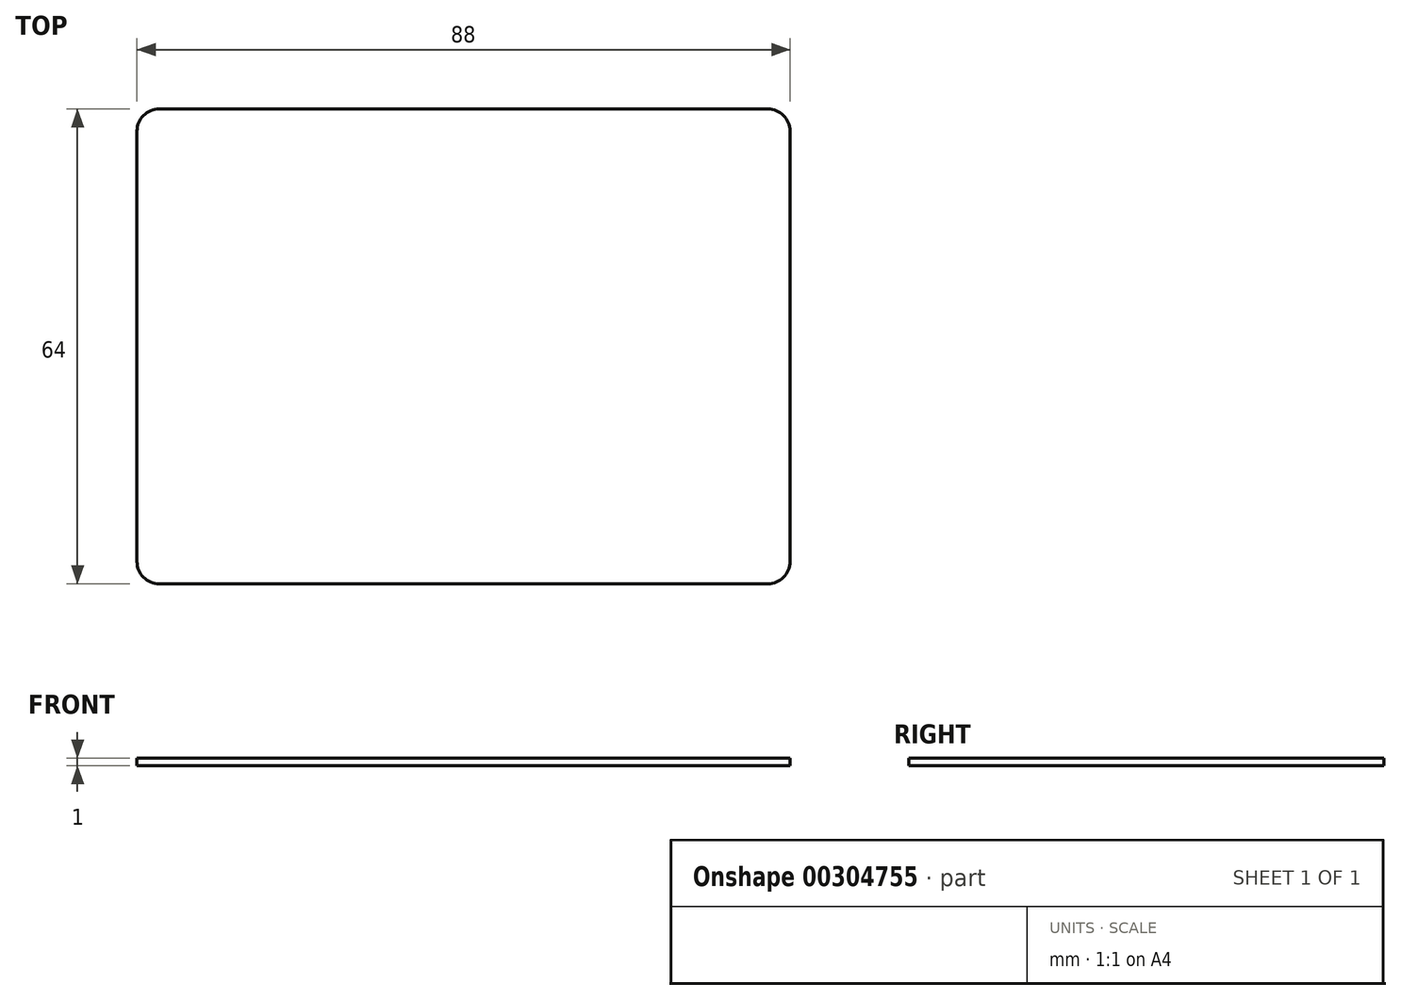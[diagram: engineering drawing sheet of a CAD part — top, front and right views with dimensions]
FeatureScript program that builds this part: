
annotation { "Feature Type Name" : "Feature", "Feature Type Description" : "" }
export const myFeature = defineFeature(function(context is Context, id is Id, definition is map)
    precondition{}
    {
        {
            var Q0;
            Q0=qCreatedBy(makeId("Top.planeOp"),FACE);
            var sketch = newSketch(context, id + "F0", { "sketchPlane" : qUnion([Q0])});
            skLineSegment(sketch, "E0.bottom", {"start": v(41, -32) * mm, "end": v(-41, -32) * mm});
            skLineSegment(sketch, "E0.top", {"start": v(41, 32) * mm, "end": v(-41, 32) * mm});
            skLineSegment(sketch, "E0.left", {"start": v(44, -29) * mm, "end": v(44, 29) * mm});
            skLineSegment(sketch, "E0.right", {"start": v(-44, -29) * mm, "end": v(-44, 29) * mm});
            skPoint(sketch, "E0.middle", {"position": v(0, 0) * mm});
            skPoint(sketch, "E1.visualSharp", {"position": v(-44, 32) * mm});
            skArc(sketch, "E1.filletArc", {"start": v(-41, 32) * mm, "mid": v(-43.12, 31.12) * mm, "end": v(-44, 29) * mm});
            skPoint(sketch, "E2.visualSharp", {"position": v(-44, -32) * mm});
            skArc(sketch, "E2.filletArc", {"start": v(-44, -29) * mm, "mid": v(-43.12, -31.12) * mm, "end": v(-41, -32) * mm});
            skPoint(sketch, "E3.visualSharp", {"position": v(44, -32) * mm});
            skArc(sketch, "E3.filletArc", {"start": v(41, -32) * mm, "mid": v(43.12, -31.12) * mm, "end": v(44, -29) * mm});
            skPoint(sketch, "E4.visualSharp", {"position": v(44, 32) * mm});
            skArc(sketch, "E4.filletArc", {"start": v(44, 29) * mm, "mid": v(43.12, 31.12) * mm, "end": v(41, 32) * mm});
            skSolve(sketch);
        }
        {
            var Q0;
            Q0=makeQuery(id+"F0.imprint","IMPRINT",FACE,{"disambiguationData":[TD([[makeQuery(id+"F0.imprint","IMPRINT",EDGE,{"derivedFrom":sQuery(id+"F0.wireOp",EDGE,"E0.bottom")}),-1.0]])]});
            extrude(context, id + "F1", {"entities" : qUnion([Q0]), "depth" : 1 * mm});
        }
    });
